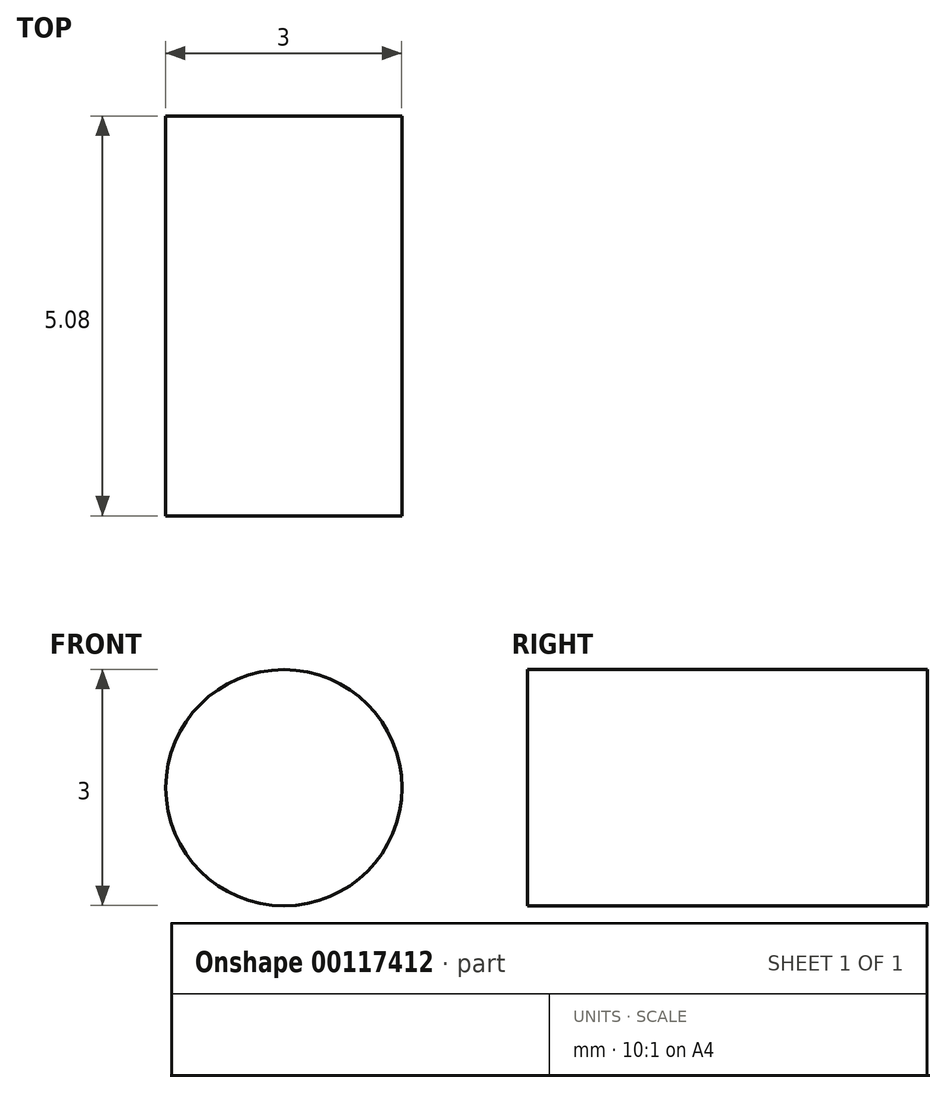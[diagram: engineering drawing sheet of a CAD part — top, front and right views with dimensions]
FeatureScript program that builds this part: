
annotation { "Feature Type Name" : "Feature", "Feature Type Description" : "" }
export const myFeature = defineFeature(function(context is Context, id is Id, definition is map)
    precondition{}
    {
        {
            var Q0;
            Q0=qCreatedBy(makeId("Front.planeOp"),FACE);
            var sketch = newSketch(context, id + "F0", { "sketchPlane" : qUnion([Q0])});
            skCircle(sketch, "E0", {"center": v(18.68, 12.5) * mm, "radius": 1.5 * mm});
            skSolve(sketch);
        }
        {
            var Q0;
            Q0=makeQuery(id+"F0.imprint","IMPRINT",FACE,{"disambiguationData":[TD([[makeQuery(id+"F0.imprint","IMPRINT",EDGE,{"derivedFrom":sQuery(id+"F0.wireOp",EDGE,"E0")}),1.0]])]});
            extrude(context, id + "F1", {"entities" : qUnion([Q0]), "depth" : 5.08 * mm});
        }
    });
